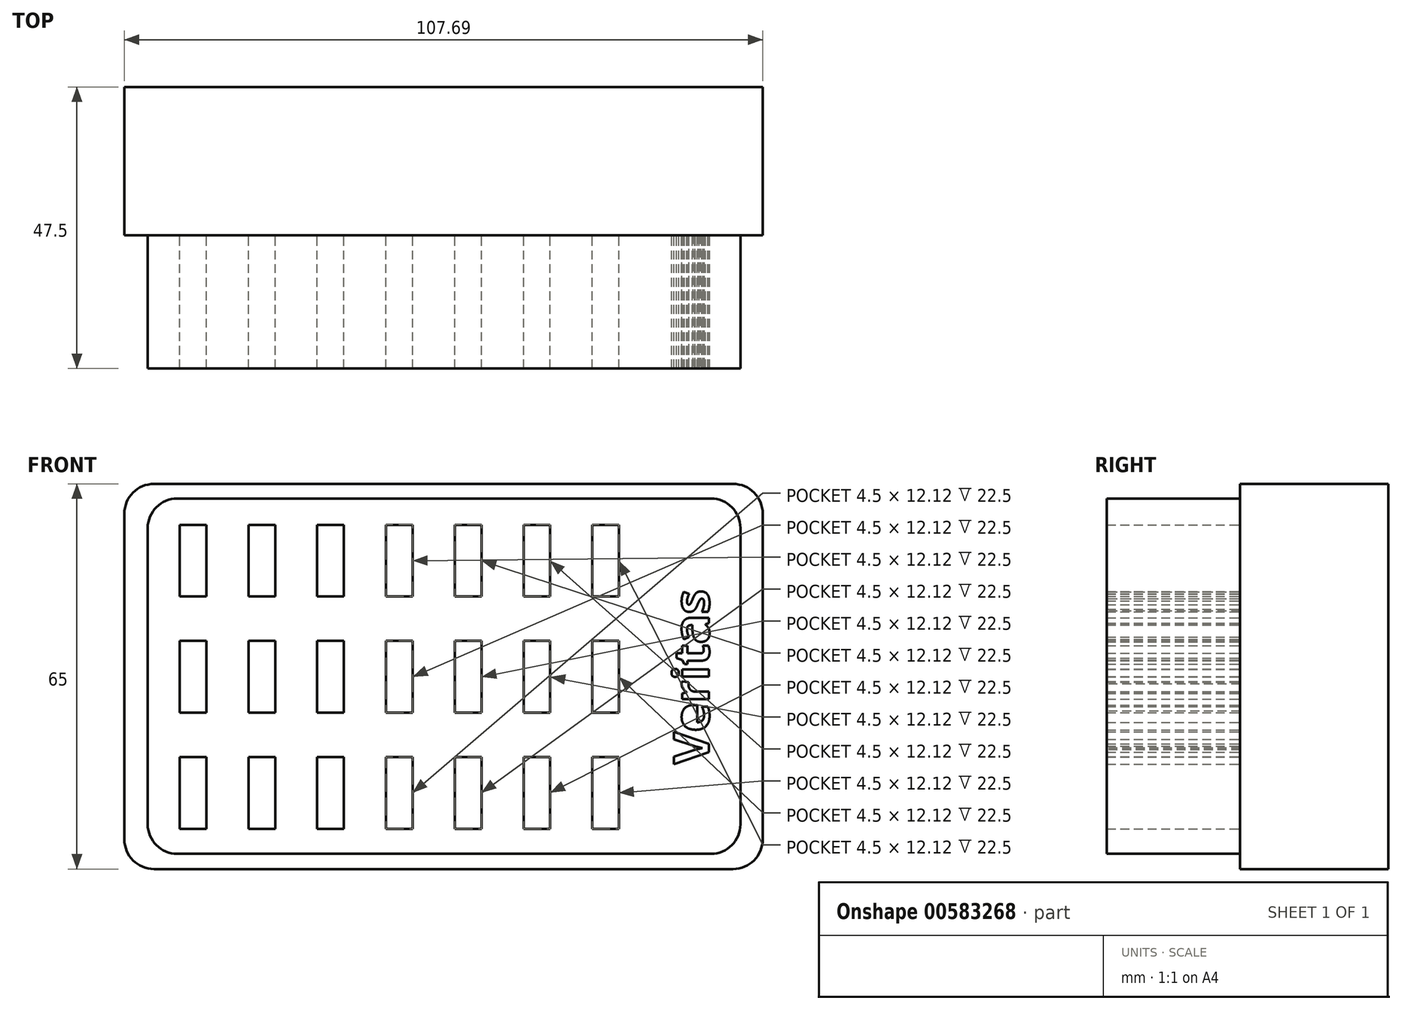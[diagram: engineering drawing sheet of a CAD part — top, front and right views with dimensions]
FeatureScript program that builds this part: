
annotation { "Feature Type Name" : "Feature", "Feature Type Description" : "" }
export const myFeature = defineFeature(function(context is Context, id is Id, definition is map)
    precondition{}
    {
        {
            var Q0;
            Q0=qCreatedBy(makeId("Front.planeOp"),FACE);
            var sketch = newSketch(context, id + "F0", { "sketchPlane" : qUnion([Q0])});
            skLineSegment(sketch, "E0.bottom", {"start": v(50, 30) * mm, "end": v(-50, 30) * mm});
            skLineSegment(sketch, "E0.top", {"start": v(50, -30) * mm, "end": v(-50, -30) * mm});
            skLineSegment(sketch, "E0.left", {"start": v(50, 30) * mm, "end": v(50, -30) * mm});
            skLineSegment(sketch, "E0.right", {"start": v(-50, 30) * mm, "end": v(-50, -30) * mm});
            skPoint(sketch, "E0.middle", {"position": v(0, 0) * mm});
            skLineSegment(sketch, "E1.bottom", {"start": v(-44.6, -13.64) * mm, "end": v(-40.1, -13.64) * mm});
            skLineSegment(sketch, "E1.top", {"start": v(-44.6, -25.76) * mm, "end": v(-40.1, -25.76) * mm});
            skLineSegment(sketch, "E1.left", {"start": v(-44.6, -13.64) * mm, "end": v(-44.6, -25.76) * mm});
            skLineSegment(sketch, "E1.right", {"start": v(-40.1, -13.64) * mm, "end": v(-40.1, -25.76) * mm});
            skLineSegment(sketch, "E2.0.1.0", {"start": v(-40.1, 5.96) * mm, "end": v(-40.1, -6.16) * mm});
            skLineSegment(sketch, "E2.0.1.1", {"start": v(-44.6, 5.96) * mm, "end": v(-44.6, -6.16) * mm});
            skLineSegment(sketch, "E2.0.1.2", {"start": v(-44.6, -6.16) * mm, "end": v(-40.1, -6.16) * mm});
            skLineSegment(sketch, "E2.0.1.3", {"start": v(-44.6, 5.96) * mm, "end": v(-40.1, 5.96) * mm});
            skLineSegment(sketch, "E2.0.2.0", {"start": v(-40.1, 25.56) * mm, "end": v(-40.1, 13.44) * mm});
            skLineSegment(sketch, "E2.0.2.1", {"start": v(-44.6, 25.56) * mm, "end": v(-44.6, 13.44) * mm});
            skLineSegment(sketch, "E2.0.2.2", {"start": v(-44.6, 13.44) * mm, "end": v(-40.1, 13.44) * mm});
            skLineSegment(sketch, "E2.0.2.3", {"start": v(-44.6, 25.56) * mm, "end": v(-40.1, 25.56) * mm});
            skLineSegment(sketch, "E2.1.0.0", {"start": v(-28.5, -13.64) * mm, "end": v(-28.5, -25.76) * mm});
            skLineSegment(sketch, "E2.1.0.1", {"start": v(-33, -13.64) * mm, "end": v(-33, -25.76) * mm});
            skLineSegment(sketch, "E2.1.0.2", {"start": v(-33, -25.76) * mm, "end": v(-28.5, -25.76) * mm});
            skLineSegment(sketch, "E2.1.0.3", {"start": v(-33, -13.64) * mm, "end": v(-28.5, -13.64) * mm});
            skLineSegment(sketch, "E2.1.1.0", {"start": v(-28.5, 5.96) * mm, "end": v(-28.5, -6.16) * mm});
            skLineSegment(sketch, "E2.1.1.1", {"start": v(-33, 5.96) * mm, "end": v(-33, -6.16) * mm});
            skLineSegment(sketch, "E2.1.1.2", {"start": v(-33, -6.16) * mm, "end": v(-28.5, -6.16) * mm});
            skLineSegment(sketch, "E2.1.1.3", {"start": v(-33, 5.96) * mm, "end": v(-28.5, 5.96) * mm});
            skLineSegment(sketch, "E2.1.2.0", {"start": v(-28.5, 25.56) * mm, "end": v(-28.5, 13.44) * mm});
            skLineSegment(sketch, "E2.1.2.1", {"start": v(-33, 25.56) * mm, "end": v(-33, 13.44) * mm});
            skLineSegment(sketch, "E2.1.2.2", {"start": v(-33, 13.44) * mm, "end": v(-28.5, 13.44) * mm});
            skLineSegment(sketch, "E2.1.2.3", {"start": v(-33, 25.56) * mm, "end": v(-28.5, 25.56) * mm});
            skLineSegment(sketch, "E2.2.0.0", {"start": v(-16.9, -13.64) * mm, "end": v(-16.9, -25.76) * mm});
            skLineSegment(sketch, "E2.2.0.1", {"start": v(-21.4, -13.64) * mm, "end": v(-21.4, -25.76) * mm});
            skLineSegment(sketch, "E2.2.0.2", {"start": v(-21.4, -25.76) * mm, "end": v(-16.9, -25.76) * mm});
            skLineSegment(sketch, "E2.2.0.3", {"start": v(-21.4, -13.64) * mm, "end": v(-16.9, -13.64) * mm});
            skLineSegment(sketch, "E2.2.1.0", {"start": v(-16.9, 5.96) * mm, "end": v(-16.9, -6.16) * mm});
            skLineSegment(sketch, "E2.2.1.1", {"start": v(-21.4, 5.96) * mm, "end": v(-21.4, -6.16) * mm});
            skLineSegment(sketch, "E2.2.1.2", {"start": v(-21.4, -6.16) * mm, "end": v(-16.9, -6.16) * mm});
            skLineSegment(sketch, "E2.2.1.3", {"start": v(-21.4, 5.96) * mm, "end": v(-16.9, 5.96) * mm});
            skLineSegment(sketch, "E2.2.2.0", {"start": v(-16.9, 25.56) * mm, "end": v(-16.9, 13.44) * mm});
            skLineSegment(sketch, "E2.2.2.1", {"start": v(-21.4, 25.56) * mm, "end": v(-21.4, 13.44) * mm});
            skLineSegment(sketch, "E2.2.2.2", {"start": v(-21.4, 13.44) * mm, "end": v(-16.9, 13.44) * mm});
            skLineSegment(sketch, "E2.2.2.3", {"start": v(-21.4, 25.56) * mm, "end": v(-16.9, 25.56) * mm});
            skLineSegment(sketch, "E2.3.0.0", {"start": v(-5.3, -13.64) * mm, "end": v(-5.3, -25.76) * mm});
            skLineSegment(sketch, "E2.3.0.1", {"start": v(-9.8, -13.64) * mm, "end": v(-9.8, -25.76) * mm});
            skLineSegment(sketch, "E2.3.0.2", {"start": v(-9.8, -25.76) * mm, "end": v(-5.3, -25.76) * mm});
            skLineSegment(sketch, "E2.3.0.3", {"start": v(-9.8, -13.64) * mm, "end": v(-5.3, -13.64) * mm});
            skLineSegment(sketch, "E2.3.1.0", {"start": v(-5.3, 5.96) * mm, "end": v(-5.3, -6.16) * mm});
            skLineSegment(sketch, "E2.3.1.1", {"start": v(-9.8, 5.96) * mm, "end": v(-9.8, -6.16) * mm});
            skLineSegment(sketch, "E2.3.1.2", {"start": v(-9.8, -6.16) * mm, "end": v(-5.3, -6.16) * mm});
            skLineSegment(sketch, "E2.3.1.3", {"start": v(-9.8, 5.96) * mm, "end": v(-5.3, 5.96) * mm});
            skLineSegment(sketch, "E2.3.2.0", {"start": v(-5.3, 25.56) * mm, "end": v(-5.3, 13.44) * mm});
            skLineSegment(sketch, "E2.3.2.1", {"start": v(-9.8, 25.56) * mm, "end": v(-9.8, 13.44) * mm});
            skLineSegment(sketch, "E2.3.2.2", {"start": v(-9.8, 13.44) * mm, "end": v(-5.3, 13.44) * mm});
            skLineSegment(sketch, "E2.3.2.3", {"start": v(-9.8, 25.56) * mm, "end": v(-5.3, 25.56) * mm});
            skLineSegment(sketch, "E2.4.0.0", {"start": v(6.3, -13.64) * mm, "end": v(6.3, -25.76) * mm});
            skLineSegment(sketch, "E2.4.0.1", {"start": v(1.8, -13.64) * mm, "end": v(1.8, -25.76) * mm});
            skLineSegment(sketch, "E2.4.0.2", {"start": v(1.8, -25.76) * mm, "end": v(6.3, -25.76) * mm});
            skLineSegment(sketch, "E2.4.0.3", {"start": v(1.8, -13.64) * mm, "end": v(6.3, -13.64) * mm});
            skLineSegment(sketch, "E2.4.1.0", {"start": v(6.3, 5.96) * mm, "end": v(6.3, -6.16) * mm});
            skLineSegment(sketch, "E2.4.1.1", {"start": v(1.8, 5.96) * mm, "end": v(1.8, -6.16) * mm});
            skLineSegment(sketch, "E2.4.1.2", {"start": v(1.8, -6.16) * mm, "end": v(6.3, -6.16) * mm});
            skLineSegment(sketch, "E2.4.1.3", {"start": v(1.8, 5.96) * mm, "end": v(6.3, 5.96) * mm});
            skLineSegment(sketch, "E2.4.2.0", {"start": v(6.3, 25.56) * mm, "end": v(6.3, 13.44) * mm});
            skLineSegment(sketch, "E2.4.2.1", {"start": v(1.8, 25.56) * mm, "end": v(1.8, 13.44) * mm});
            skLineSegment(sketch, "E2.4.2.2", {"start": v(1.8, 13.44) * mm, "end": v(6.3, 13.44) * mm});
            skLineSegment(sketch, "E2.4.2.3", {"start": v(1.8, 25.56) * mm, "end": v(6.3, 25.56) * mm});
            skLineSegment(sketch, "E2.5.0.0", {"start": v(17.9, -13.64) * mm, "end": v(17.9, -25.76) * mm});
            skLineSegment(sketch, "E2.5.0.1", {"start": v(13.4, -13.64) * mm, "end": v(13.4, -25.76) * mm});
            skLineSegment(sketch, "E2.5.0.2", {"start": v(13.4, -25.76) * mm, "end": v(17.9, -25.76) * mm});
            skLineSegment(sketch, "E2.5.0.3", {"start": v(13.4, -13.64) * mm, "end": v(17.9, -13.64) * mm});
            skLineSegment(sketch, "E2.5.1.0", {"start": v(17.9, 5.96) * mm, "end": v(17.9, -6.16) * mm});
            skLineSegment(sketch, "E2.5.1.1", {"start": v(13.4, 5.96) * mm, "end": v(13.4, -6.16) * mm});
            skLineSegment(sketch, "E2.5.1.2", {"start": v(13.4, -6.16) * mm, "end": v(17.9, -6.16) * mm});
            skLineSegment(sketch, "E2.5.1.3", {"start": v(13.4, 5.96) * mm, "end": v(17.9, 5.96) * mm});
            skLineSegment(sketch, "E2.5.2.0", {"start": v(17.9, 25.56) * mm, "end": v(17.9, 13.44) * mm});
            skLineSegment(sketch, "E2.5.2.1", {"start": v(13.4, 25.56) * mm, "end": v(13.4, 13.44) * mm});
            skLineSegment(sketch, "E2.5.2.2", {"start": v(13.4, 13.44) * mm, "end": v(17.9, 13.44) * mm});
            skLineSegment(sketch, "E2.5.2.3", {"start": v(13.4, 25.56) * mm, "end": v(17.9, 25.56) * mm});
            skLineSegment(sketch, "E2.6.0.0", {"start": v(29.5, -13.64) * mm, "end": v(29.5, -25.76) * mm});
            skLineSegment(sketch, "E2.6.0.1", {"start": v(25, -13.64) * mm, "end": v(25, -25.76) * mm});
            skLineSegment(sketch, "E2.6.0.2", {"start": v(25, -25.76) * mm, "end": v(29.5, -25.76) * mm});
            skLineSegment(sketch, "E2.6.0.3", {"start": v(25, -13.64) * mm, "end": v(29.5, -13.64) * mm});
            skLineSegment(sketch, "E2.6.1.0", {"start": v(29.5, 5.96) * mm, "end": v(29.5, -6.16) * mm});
            skLineSegment(sketch, "E2.6.1.1", {"start": v(25, 5.96) * mm, "end": v(25, -6.16) * mm});
            skLineSegment(sketch, "E2.6.1.2", {"start": v(25, -6.16) * mm, "end": v(29.5, -6.16) * mm});
            skLineSegment(sketch, "E2.6.1.3", {"start": v(25, 5.96) * mm, "end": v(29.5, 5.96) * mm});
            skLineSegment(sketch, "E2.6.2.0", {"start": v(29.5, 25.56) * mm, "end": v(29.5, 13.44) * mm});
            skLineSegment(sketch, "E2.6.2.1", {"start": v(25, 25.56) * mm, "end": v(25, 13.44) * mm});
            skLineSegment(sketch, "E2.6.2.2", {"start": v(25, 13.44) * mm, "end": v(29.5, 13.44) * mm});
            skLineSegment(sketch, "E2.6.2.3", {"start": v(25, 25.56) * mm, "end": v(29.5, 25.56) * mm});
            skLineSegment(sketch, "E2.direction1", {"start": v(-44.6, -25.76) * mm, "end": v(-33, -25.76) * mm, "construction": true});
            skLineSegment(sketch, "E2.direction2", {"start": v(-44.6, -25.76) * mm, "end": v(-44.6, -6.16) * mm, "construction": true});
            skText(sketch, "E3", { "text": "Veritas\n", "fontName": "OpenSans-Bold.ttf"});
            const initialGuessF0  = {"E3": [0.0447, -0.01484, 0, 1, 0.006]};
            skSetInitialGuess(sketch, initialGuessF0);
            skSolve(sketch);
        }
        {
            var Q0;
            Q0=makeQuery(id+"F0.imprint","IMPRINT",FACE,{"disambiguationData":[TD([[makeQuery(id+"F0.imprint","IMPRINT",EDGE,{"derivedFrom":sQuery(id+"F0.wireOp",EDGE,"E0.bottom")}),1.0]])]});
            extrude(context, id + "F1", {"entities" : qUnion([Q0]), "depth" : 35 * mm, "offsetDistance" : 25 * mm});
        }
        {
            var Q0;
            Q0=qCreatedBy(makeId("Front.planeOp"),FACE);
            var sketch = newSketch(context, id + "F2", { "sketchPlane" : qUnion([Q0])});
            skLineSegment(sketch, "E4.bottom", {"start": v(53.75, 32.45) * mm, "end": v(-53.94, 32.45) * mm});
            skLineSegment(sketch, "E4.top", {"start": v(53.75, -32.55) * mm, "end": v(-53.94, -32.55) * mm});
            skLineSegment(sketch, "E4.left", {"start": v(53.75, 32.45) * mm, "end": v(53.75, -32.55) * mm});
            skLineSegment(sketch, "E4.right", {"start": v(-53.94, 32.45) * mm, "end": v(-53.94, -32.55) * mm});
            skSolve(sketch);
        }
        {
            var Q0;
            Q0 = qSketchRegion(id + "F2", true);
            extrude(context, id + "F3", {"entities" : qUnion([Q0]), "operationType" : NewBodyOperationType.ADD, "endBound" : BoundingType.SYMMETRIC, "depth" : 25 * mm, "offsetDistance" : 25 * mm});
        }
        {
            var Q0;
            Q0=makeQuery(id+"F1.opExtrude","SWEPT_EDGE",EDGE,{"disambiguationData":[OSD([sQuery(id+"F0.wireOp",EDGE,"E0.top"),sQuery(id+"F0.wireOp",EDGE,"E0.right")])]});
            var Q1;
            Q1=makeQuery(id+"F1.opExtrude","SWEPT_EDGE",EDGE,{"disambiguationData":[OSD([sQuery(id+"F0.wireOp",EDGE,"E0.top"),sQuery(id+"F0.wireOp",EDGE,"E0.left")])]});
            var Q2;
            Q2=makeQuery(id+"F1.opExtrude","SWEPT_EDGE",EDGE,{"disambiguationData":[OSD([sQuery(id+"F0.wireOp",EDGE,"E0.bottom"),sQuery(id+"F0.wireOp",EDGE,"E0.left")])]});
            var Q3;
            Q3=makeQuery(id+"F1.opExtrude","SWEPT_EDGE",EDGE,{"disambiguationData":[OSD([sQuery(id+"F0.wireOp",EDGE,"E0.bottom"),sQuery(id+"F0.wireOp",EDGE,"E0.right")])]});
            var Q4;
            Q4=makeQuery(id+"F3.opExtrude","SWEPT_EDGE",EDGE,{"disambiguationData":[OSD([sQuery(id+"F2.wireOp",EDGE,"E4.top"),sQuery(id+"F2.wireOp",EDGE,"E4.right")])]});
            var Q5;
            Q5=makeQuery(id+"F3.opExtrude","SWEPT_EDGE",EDGE,{"disambiguationData":[OSD([sQuery(id+"F2.wireOp",EDGE,"E4.top"),sQuery(id+"F2.wireOp",EDGE,"E4.left")])]});
            var Q6;
            Q6=makeQuery(id+"F3.opExtrude","SWEPT_EDGE",EDGE,{"disambiguationData":[OSD([sQuery(id+"F2.wireOp",EDGE,"E4.bottom"),sQuery(id+"F2.wireOp",EDGE,"E4.left")])]});
            var Q7;
            Q7=makeQuery(id+"F3.opExtrude","SWEPT_EDGE",EDGE,{"disambiguationData":[OSD([sQuery(id+"F2.wireOp",EDGE,"E4.bottom"),sQuery(id+"F2.wireOp",EDGE,"E4.right")])]});
            fillet(context, id + "F4", {"entities" : qUnion([Q0, Q1, Q2, Q3, Q4, Q5, Q6, Q7]), "radius" : 5 * mm, "tangentPropagation" : true, "allowEdgeOverflow" : false});
        }
    });
